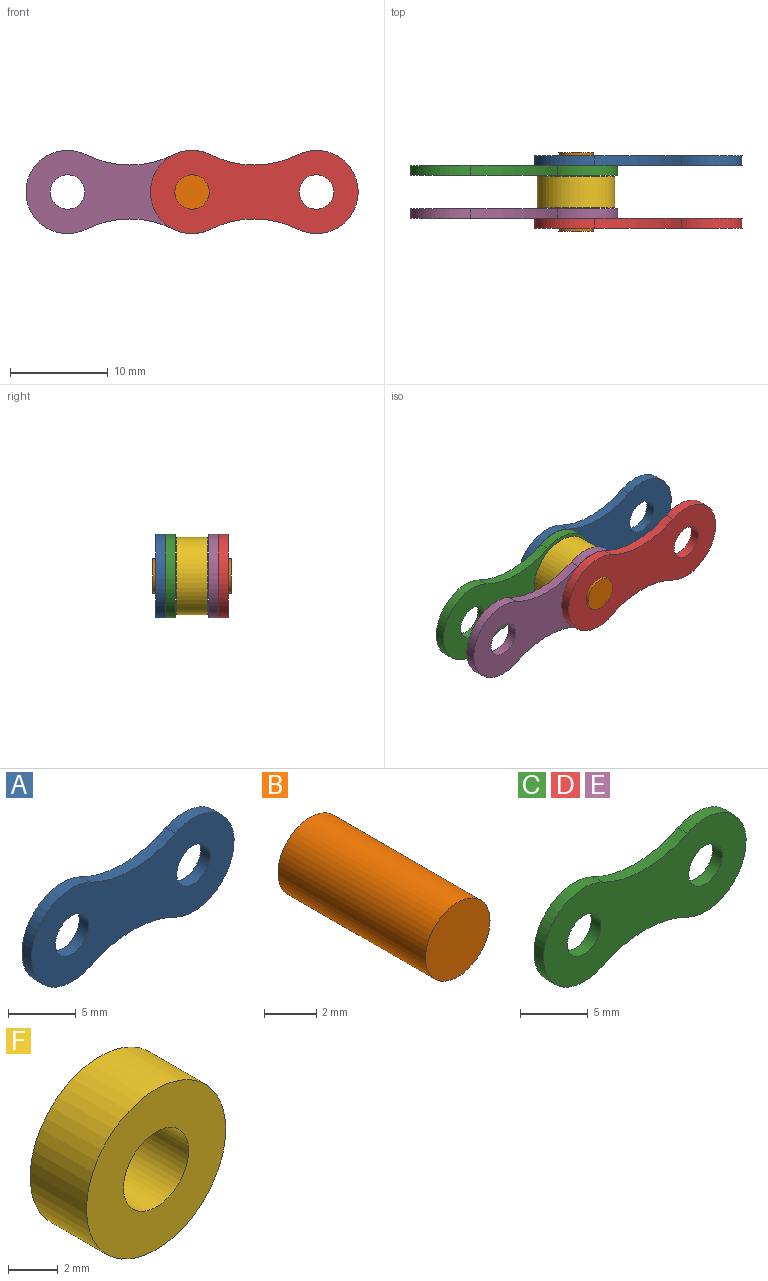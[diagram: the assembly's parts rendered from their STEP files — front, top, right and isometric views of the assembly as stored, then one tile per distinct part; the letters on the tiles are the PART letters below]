
ASSEMBLY  parts=6 mates=5
PART A: 8 faces, bbox 21.2x1x8.5 mm
  f0: cylinder r=4.25mm len=8.5mm, axis (0,-1,0), area 17.3mm2, adj f1,f4,f6,f7
  f1: cylinder r=9.94mm len=8.9mm, axis (0,-1,0), area 9.2mm2, adj f0,f2,f6,f7
  f2: cylinder r=4.25mm len=8.5mm, axis (0,-1,0), area 17.3mm2, adj f1,f4,f6,f7
  f3: cylinder r=1.75mm len=3.5mm, axis (0,-1,0), area 11mm2, adj f6,f7
  f4: cylinder r=9.94mm len=8.9mm, axis (0,-1,0), area 9.2mm2, adj f0,f2,f6,f7
  f5: cylinder r=1.75mm len=3.5mm, axis (0,-1,0), area 11mm2, adj f6,f7
  f6: plane 21.2x8.5mm, normal (0,1,0), area 123.7mm2, adj f0,f1,f2,f3,f4,f5
  f7: plane 21.2x8.5mm, normal (0,-1,0), area 123.7mm2, adj f0,f1,f2,f3,f4,f5
PART B: 3 faces, bbox 3.5x8x3.5 mm
  f0: cylinder r=1.75mm len=8mm, axis (0,1,0), area 88mm2, adj f1,f2
  f1: plane 3.5x3.5mm, normal (0,-1,0), area 9.6mm2, adj f0
  f2: plane 3.5x3.5mm, normal (0,1,0), area 9.6mm2, adj f0
PART C: 8 faces, bbox 21.2x1x8.5 mm
  f0: cylinder r=4.25mm len=8.5mm, axis (0,1,0), area 17.3mm2, adj f1,f4,f6,f7
  f1: cylinder r=9.94mm len=8.9mm, axis (0,1,0), area 9.2mm2, adj f0,f2,f6,f7
  f2: cylinder r=4.25mm len=8.5mm, axis (0,1,0), area 17.3mm2, adj f1,f4,f6,f7
  f3: cylinder r=1.75mm len=3.5mm, axis (0,1,0), area 11mm2, adj f6,f7
  f4: cylinder r=9.94mm len=8.9mm, axis (0,1,0), area 9.2mm2, adj f0,f2,f6,f7
  f5: cylinder r=1.75mm len=3.5mm, axis (0,1,0), area 11mm2, adj f6,f7
  f6: plane 21.2x8.5mm, normal (0,-1,0), area 123.7mm2, adj f0,f1,f2,f3,f4,f5
  f7: plane 21.2x8.5mm, normal (0,1,0), area 123.7mm2, adj f0,f1,f2,f3,f4,f5
PART D: same geometry as C
PART E: same geometry as C
PART F: 4 faces, bbox 7.9x3.2x7.9 mm
  f0: cylinder r=1.85mm len=3.7mm, axis (0,-1,0), area 37.2mm2, adj f2,f3
  f1: cylinder r=3.95mm len=7.9mm, axis (0,-1,0), area 79.4mm2, adj f2,f3
  f2: plane 7.9x7.9mm, normal (0,1,0), area 38.3mm2, adj f0,f1
  f3: plane 7.9x7.9mm, normal (0,-1,0), area 38.3mm2, adj f0,f1
PLACE A t=(0.91,0.02,-2.84)mm
PLACE B t=(0.91,-1.08,-2.84)mm
PLACE C t=(-11.79,3.22,-2.84)mm
PLACE D t=(0.91,-2.18,-2.84)mm
PLACE E t=(-11.79,-1.18,-2.84)mm
PLACE F t=(0.91,-1.08,-2.84)mm
MATE revolute D.f2 <-> E.f0  axis (0,1,0) through (-5.44,-3.78,-2.84)mm
MATE revolute A.f2 <-> C.f0  axis (0,-1,0) through (-5.44,1.62,-2.84)mm
MATE fastened B.f0 <-> D.f2  axis (0,-1,0) through (-5.44,-5.08,-2.84)mm
MATE revolute F.f0 <-> B.f0  axis (0,-1,0) through (-5.44,-1.08,-2.84)mm
MATE fastened A.f2 <-> B.f0  axis (0,1,0) through (-5.44,2.62,-2.84)mm
